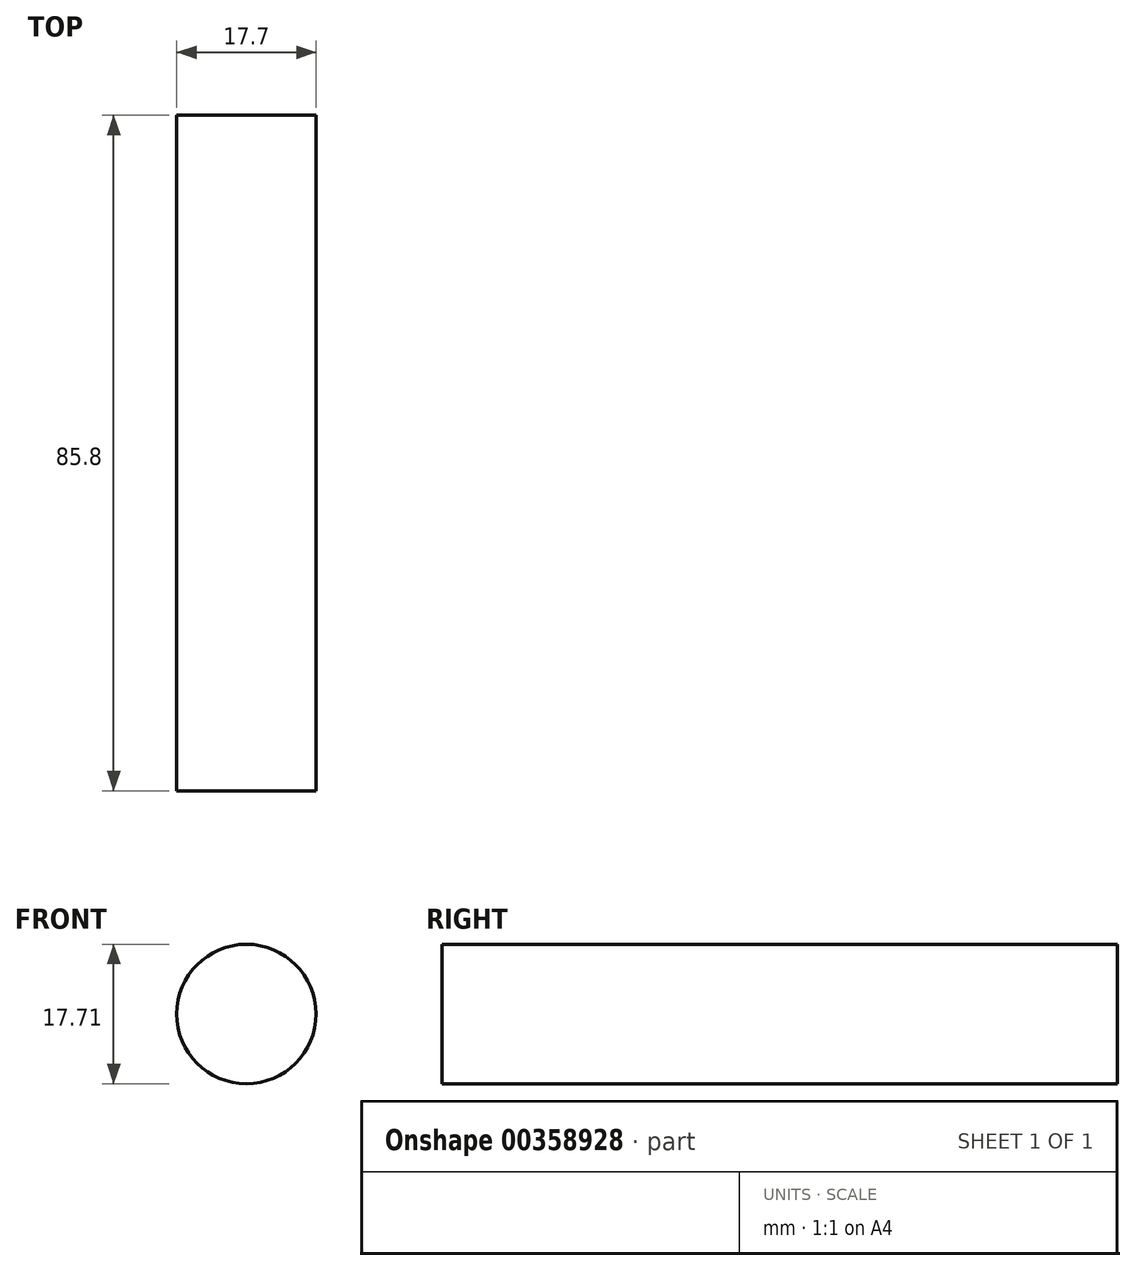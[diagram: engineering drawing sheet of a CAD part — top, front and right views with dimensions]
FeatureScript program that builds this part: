
annotation { "Feature Type Name" : "Feature", "Feature Type Description" : "" }
export const myFeature = defineFeature(function(context is Context, id is Id, definition is map)
    precondition{}
    {
        {
            var Q0;
            Q0=qCreatedBy(makeId("Front.planeOp"),FACE);
            var sketch = newSketch(context, id + "F0", { "sketchPlane" : qUnion([Q0])});
            skCircle(sketch, "E0", {"center": v(-65.16, -10.87) * mm, "radius": 8.85 * mm});
            skSolve(sketch);
        }
        {
            var Q0;
            Q0 = qSketchRegion(id + "F0", true);
            extrude(context, id + "F1", {"entities" : qUnion([Q0]), "depth" : 85.8 * mm});
        }
    });
